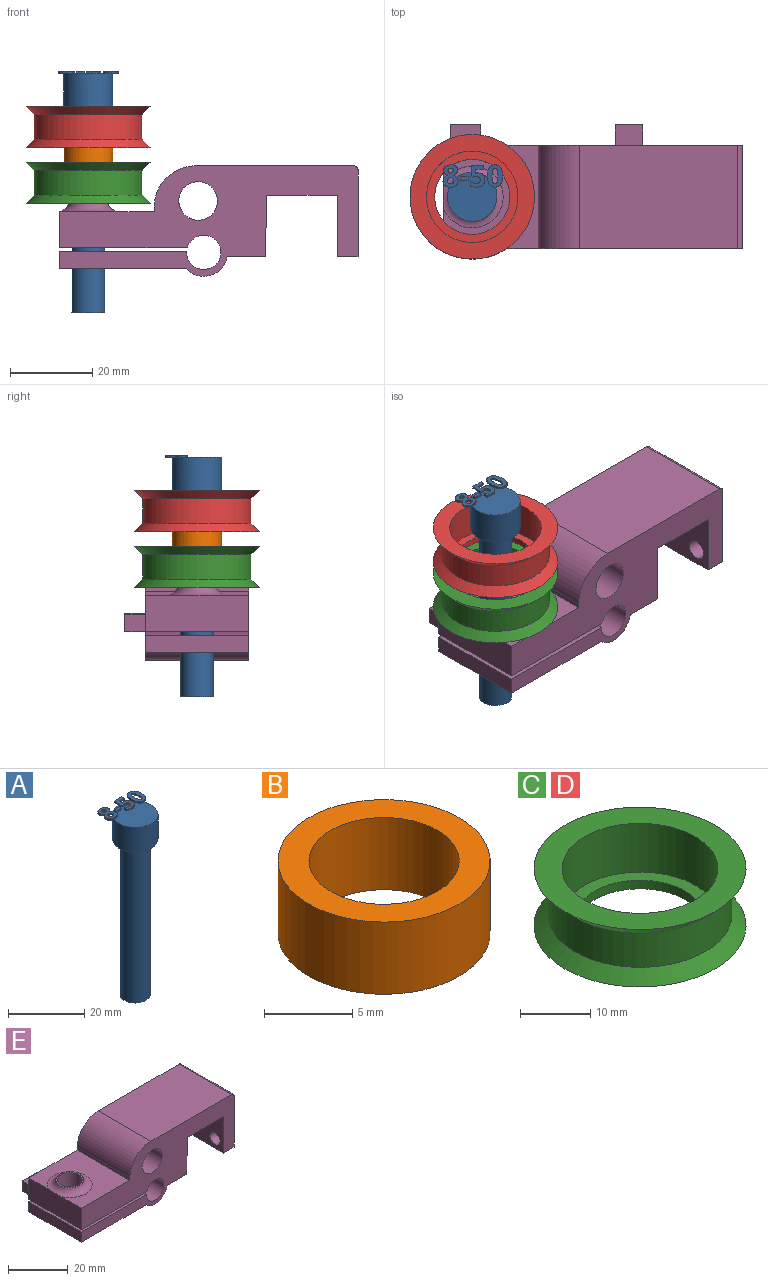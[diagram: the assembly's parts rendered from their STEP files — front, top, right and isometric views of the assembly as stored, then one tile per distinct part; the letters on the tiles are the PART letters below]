
ASSEMBLY  parts=5 mates=4
PART A: 86 faces, bbox 14.5x13.7x58.5 mm
  f0: plane 12x12mm, normal (0,0,1), area 99.4mm2, adj f5,f22,f23,f24,f25,f26,f40,f41
  f1: plane 1x0.26mm, normal (0,0,1), area 0.1mm2, adj f5,f46,f47,f48,f49
  f2: plane 0.85x0.68mm, normal (0,0,1), area 0.2mm2, adj f5,f29,f30,f31
  f3: cylinder r=4mm len=50mm, axis (0,0,-1), area 1256.6mm2, adj f4,f6
  f4: plane 8x8mm, normal (0,0,-1), area 50.3mm2, adj f3
  f5: cylinder r=6mm len=12mm, axis (0,0,-1), area 301.6mm2, adj f0,f1,f2,f6,f39,f45,f67,f85
  f6: plane 12x12mm, normal (0,0,-1), area 62.8mm2, adj f3,f5
  f7: extruded ~0.5x0.46mm, area 0.2mm2, adj f8,f37,f38,f39
  f8: extruded ~0.5x0.46mm, area 0.2mm2, adj f7,f9,f38,f39
  f9: extruded ~0.5x0.39mm, area 0.2mm2, adj f8,f10,f38,f39
  f10: extruded ~0.5x0.4mm, area 0.2mm2, adj f9,f11,f38,f39
  f11: extruded ~0.5x0.49mm, area 0.3mm2, adj f10,f12,f38,f39
  f12: extruded ~0.5x0.5mm, area 0.3mm2, adj f11,f13,f38,f39
  f13: extruded ~0.5x0.39mm, area 0.2mm2, adj f12,f37,f38,f39
  f14: extruded ~1.22x0.5mm, area 0.6mm2, adj f15,f35,f38,f39
  f15: extruded ~1.22x0.5mm, area 0.6mm2, adj f14,f16,f38,f39
  f16: extruded ~0.91x0.5mm, area 0.5mm2, adj f15,f17,f38,f39
  f17: extruded ~0.71x0.5mm, area 0.4mm2, adj f16,f18,f38,f39
  f18: extruded ~0.65x0.61mm, area 0.4mm2, adj f17,f19,f38,f39
  f19: extruded ~0.77x0.62mm, area 0.5mm2, adj f18,f20,f38,f39
  f20: extruded ~0.8x0.5mm, area 0.4mm2, adj f19,f21,f38,f39
  f21: extruded ~1.04x0.5mm, area 0.6mm2, adj f20,f22,f38,f39
  f22: extruded ~1.36x0.5mm, area 0.7mm2, adj f0,f21,f23,f38,f39
  f23: extruded ~1.33x0.5mm, area 0.7mm2, adj f0,f22,f24,f38
  f24: extruded ~1.04x0.51mm, area 0.6mm2, adj f0,f23,f25,f38
  f25: extruded ~0.75x0.5mm, area 0.4mm2, adj f0,f24,f26,f38
  f26: extruded ~0.85x0.66mm, area 0.5mm2, adj f0,f25,f27,f38,f39
  f27: extruded ~0.72x0.56mm, area 0.5mm2, adj f26,f28,f38,f39
  f28: extruded ~0.72x0.5mm, area 0.4mm2, adj f27,f35,f38,f39
  f29: extruded ~0.5x0.45mm, area 0.3mm2, adj f2,f30,f36,f38,f39
  f30: extruded ~0.5x0.47mm, area 0.3mm2, adj f2,f29,f31,f38
  f31: extruded ~0.62x0.5mm, area 0.3mm2, adj f2,f30,f32,f38,f39
  f32: extruded ~0.59x0.5mm, area 0.3mm2, adj f31,f33,f38,f39
  f33: extruded ~0.5x0.48mm, area 0.3mm2, adj f32,f34,f38,f39
  f34: extruded ~0.89x0.77mm, area 0.6mm2, adj f33,f36,f38,f39
  f35: extruded ~0.93x0.5mm, area 0.5mm2, adj f14,f28,f38,f39
  f36: extruded ~0.66x0.5mm, area 0.4mm2, adj f29,f34,f38,f39
  f37: extruded ~0.5x0.39mm, area 0.2mm2, adj f7,f13,f38,f39
  f38: plane 5.4x3.69mm, normal (0,0,1), area 12.7mm2, adj f7,f8,f9,f10,f11,f12,f13,f14
  f39: plane 5.4x3.53mm, normal (0,0,-1), area 10.2mm2, adj f5,f7,f8,f9,f10,f11,f12,f13
  f40: plane 0.9x0.5mm, normal (-1,0,0), area 0.4mm2, adj f0,f41,f43,f44
  f41: plane 1.93x0.5mm, normal (0,-1,0), area 1mm2, adj f0,f40,f42,f44
  f42: plane 0.9x0.5mm, normal (1,0,0), area 0.4mm2, adj f0,f41,f43,f44
  f43: plane 1.93x0.5mm, normal (0,1,0), area 1mm2, adj f0,f40,f42,f44
  f44: plane 1.93x0.9mm, normal (0,0,1), area 1.7mm2, adj f40,f41,f42,f43
  f45: plane 0.76x0.31mm, normal (0,0,-1), area 0mm2, adj f5,f46
  f46: extruded ~1.21x0.5mm, area 0.7mm2, adj f0,f1,f45,f47,f65,f66
  f47: extruded ~0.54x0.5mm, area 0.3mm2, adj f1,f46,f48,f66
  f48: plane 0.5x0.13mm, normal (-0.2,0.98,0), area 0.1mm2, adj f1,f47,f49,f66
  f49: plane 1.03x0.5mm, normal (1,-0.09,0), area 0.5mm2, adj f1,f48,f50,f66,f67
  f50: plane 1.88x0.5mm, normal (0,-1,0), area 0.9mm2, adj f49,f51,f66,f67
  f51: plane 0.94x0.5mm, normal (1,0,0), area 0.5mm2, adj f50,f52,f66,f67
  f52: plane 2.85x0.5mm, normal (0,1,0), area 1.4mm2, adj f51,f53,f66,f67
  f53: plane 2.68x0.5mm, normal (-1,0.07,0), area 1.3mm2, adj f0,f52,f54,f66,f67
  f54: plane 0.5x0.44mm, normal (-0.47,-0.88,0), area 0.3mm2, adj f0,f53,f55,f66
  f55: extruded ~0.5x0.37mm, area 0.2mm2, adj f0,f54,f56,f66
  f56: extruded ~0.5x0.42mm, area 0.2mm2, adj f0,f55,f57,f66
  f57: extruded ~1.05x0.8mm, area 0.8mm2, adj f0,f56,f58,f66
  f58: extruded ~1.02x0.83mm, area 0.8mm2, adj f0,f57,f59,f66
  f59: extruded ~0.72x0.5mm, area 0.4mm2, adj f0,f58,f60,f66
  f60: extruded ~0.66x0.5mm, area 0.4mm2, adj f0,f59,f61,f66
  f61: plane 0.96x0.5mm, normal (-1,0,0), area 0.5mm2, adj f0,f60,f62,f66
  f62: extruded ~1.42x0.5mm, area 0.7mm2, adj f0,f61,f63,f66
  f63: extruded ~1.55x0.5mm, area 0.8mm2, adj f0,f62,f64,f66
  f64: extruded ~1.36x0.54mm, area 0.8mm2, adj f0,f63,f65,f66
  f65: extruded ~1.17x0.5mm, area 0.6mm2, adj f0,f46,f64,f66
  f66: plane 5.33x3.51mm, normal (0,0,1), area 10.9mm2, adj f46,f47,f48,f49,f50,f51,f52,f53
  f67: plane 2.97x1.71mm, normal (0,0,-1), area 3.5mm2, adj f5,f49,f50,f51,f52,f53
  f68: extruded ~1.39x0.5mm, area 0.7mm2, adj f69,f83,f84,f85
  f69: extruded ~1.39x0.5mm, area 0.7mm2, adj f68,f70,f84,f85
  f70: extruded ~0.56x0.5mm, area 0.4mm2, adj f69,f71,f84,f85
  f71: extruded ~0.56x0.5mm, area 0.4mm2, adj f70,f72,f84,f85
  f72: extruded ~1.39x0.5mm, area 0.7mm2, adj f71,f73,f84,f85
  f73: extruded ~1.38x0.5mm, area 0.7mm2, adj f72,f74,f84,f85
  f74: extruded ~0.56x0.5mm, area 0.4mm2, adj f73,f83,f84,f85
  f75: extruded ~2.04x0.5mm, area 1.1mm2, adj f76,f82,f84,f85
  f76: extruded ~2.02x0.5mm, area 1.1mm2, adj f75,f77,f84,f85
  f77: extruded ~1.38x0.69mm, area 0.8mm2, adj f76,f78,f84,f85
  f78: extruded ~1.38x0.66mm, area 0.8mm2, adj f77,f79,f84,f85
  f79: extruded ~2.05x0.5mm, area 1.1mm2, adj f78,f80,f84,f85
  f80: extruded ~2.02x0.5mm, area 1mm2, adj f0,f79,f81,f84,f85
  f81: extruded ~1.37x0.68mm, area 0.8mm2, adj f0,f80,f82,f84
  f82: extruded ~1.39x0.66mm, area 0.8mm2, adj f0,f75,f81,f84,f85
  f83: extruded ~0.56x0.5mm, area 0.4mm2, adj f68,f74,f84,f85
  f84: plane 5.41x3.68mm, normal (0,0,1), area 12.1mm2, adj f68,f69,f70,f71,f72,f73,f74,f75
  f85: plane 5.41x3.68mm, normal (0,0,-1), area 10.3mm2, adj f5,f68,f69,f70,f71,f72,f73,f74
PART B: 4 faces, bbox 12x12x5 mm
  f0: cylinder r=4.25mm len=8.5mm, axis (0,0,-1), area 133.5mm2, adj f2,f3
  f1: cylinder r=6mm len=12mm, axis (0,0,-1), area 188.5mm2, adj f2,f3
  f2: plane 12x12mm, normal (0,0,1), area 56.4mm2, adj f0,f1
  f3: plane 12x12mm, normal (0,0,-1), area 56.4mm2, adj f0,f1
PART C: 8 faces, bbox 30.2x30.2x10 mm
  f0: plane 30.2x30.2mm, normal (0,0,1), area 329.2mm2, adj f1,f7
  f1: cylinder r=11.1mm len=22.2mm, axis (0,0,-1), area 592.8mm2, adj f0,f2
  f2: plane 22.2x22.2mm, normal (0,0,1), area 126.9mm2, adj f1,f3
  f3: cylinder r=9.1mm len=18.2mm, axis (0,0,-1), area 85.8mm2, adj f2,f4
  f4: plane 30.2x30.2mm, normal (0,0,-1), area 456.2mm2, adj f3,f5
  f5: cone r=13.1mm half-angle=45deg, axis (0,0,-1), area 250.6mm2, adj f4,f6
  f6: cylinder r=13.1mm len=26.2mm, axis (0,0,-1), area 493.9mm2, adj f5,f7
  f7: cone r=15.1mm half-angle=45deg, axis (0,0,1), area 250.6mm2, adj f0,f6
PART D: same geometry as C
PART E: 36 faces, bbox 75.9x30x26.8 mm
  f0: plane 25x4.13mm, normal (-1,0,0), area 103.3mm2, adj f3,f13,f14,f18
  f1: cylinder r=4.17mm len=8.35mm, axis (0,0,1), area 108.4mm2, adj f3,f18
  f2: plane 25x9.29mm, normal (0,0,-1), area 232.2mm2, adj f12,f13,f14,f16
  f3: plane 30.81x25mm, normal (0,0,-1), area 715.5mm2, adj f0,f1,f13,f14,f16
  f4: plane 25x8.81mm, normal (-1,0,0), area 219.3mm2, adj f5,f13,f14,f19,f23
  f5: plane 25x23mm, normal (0,0,1), area 400mm2, adj f4,f6,f13,f14,f23
  f6: plane 25x1.1mm, normal (-1,0,0), area 27.5mm2, adj f5,f13,f14,f24
  f7: plane 38.42x25mm, normal (0,0,1), area 960.6mm2, adj f13,f14,f24,f26
  f8: plane 25x21.09mm, normal (1,0,0), area 493.5mm2, adj f9,f13,f14,f21,f22,f26
  f9: plane 25x5mm, normal (0,0,-1), area 125mm2, adj f8,f10,f13,f14
  f10: plane 25x15mm, normal (-1,0,0), area 341.3mm2, adj f9,f11,f13,f14,f21,f22
  f11: plane 25x17.2mm, normal (0,0,-1), area 430mm2, adj f10,f12,f13,f14
  f12: plane 25x14.91mm, normal (1,0,-0.01), area 372.8mm2, adj f2,f11,f13,f14
  f13: plane 72.42x26.8mm, normal (0,-1,0), area 1035.8mm2, adj f0,f2,f3,f4,f5,f6,f7,f8
  f14: plane 72.42x26.8mm, normal (0,1,0), area 975.8mm2, adj f0,f2,f3,f4,f5,f6,f7,f8
  f15: cylinder r=4.17mm len=10.77mm, axis (0,0,1), area 282.4mm2, adj f19,f20
  f16: cylinder r=5.8mm len=25mm, axis (0,-1,0), area 320.1mm2, adj f2,f3,f13,f14
  f17: cylinder r=4.15mm len=25mm, axis (0,-1,0), area 626.5mm2, adj f13,f14,f18,f19
  f18: plane 30.86x25mm, normal (0,0,1), area 716.8mm2, adj f0,f1,f13,f14,f17
  f19: plane 31.02x30mm, normal (0,0,-1), area 757.2mm2, adj f4,f13,f14,f15,f17,f28,f29,f30
  f20: plane 9.35x9.35mm, normal (0,0,1), area 13.9mm2, adj f15,f23
  f21: cylinder r=2.43mm len=5mm, axis (1,0,0), area 76.2mm2, adj f8,f10
  f22: cylinder r=2.2mm len=5mm, axis (1,0,0), area 69.1mm2, adj f8,f10
  f23: torus R=7.5mm, axis (0,0,-1), area 134.6mm2, adj f4,f5,f20
  f24: cylinder r=10mm len=25mm, axis (0,-1,0), area 392.7mm2, adj f6,f7,f13,f14
  f25: cylinder r=4.68mm len=25mm, axis (0,-1,0), area 735.2mm2, adj f13,f14
  f26: cylinder r=1mm len=25mm, axis (0,-1,0), area 39.3mm2, adj f7,f8,f13,f14
  f27: plane 7.3x5mm, normal (0,0,1), area 36.5mm2, adj f14,f28,f29,f30
  f28: plane 5x4.12mm, normal (-1,0,0), area 20.6mm2, adj f14,f19,f27,f30
  f29: plane 5x4.12mm, normal (1,0,0), area 20.6mm2, adj f14,f19,f27,f30
  f30: plane 7.3x4.12mm, normal (0,1,0), area 30.1mm2, adj f19,f27,f28,f29
  f31: plane 6.63x5mm, normal (0,0,1), area 33.2mm2, adj f14,f32,f34,f35
  f32: plane 5x4.5mm, normal (-1,0,0), area 22.5mm2, adj f14,f31,f33,f35
  f33: plane 6.63x5mm, normal (0,0,-1), area 33.2mm2, adj f14,f32,f34,f35
  f34: plane 5x4.5mm, normal (1,0,0), area 22.5mm2, adj f14,f31,f33,f35
  f35: plane 6.63x4.5mm, normal (0,1,0), area 29.9mm2, adj f31,f32,f33,f34
PLACE A t=(-103.78,-12.5,-13.6)mm
PLACE B rot(axis=(1,0,0),180deg) t=(-103.78,-12.5,26.4)mm
PLACE C t=(-103.78,-12.5,18.1)mm
PLACE D t=(-103.78,-12.5,31.6)mm
PLACE E at identity
MATE fastened A.f3 <-> D.f1  axis (0,0,-1) through (-103.78,-12.5,36.4)mm
MATE fastened B.f0 <-> C.f1  axis (0,0,1) through (-103.78,-12.5,21.4)mm
MATE fastened C.f1 <-> E.f1  axis (0,0,-1) through (-103.78,-12.5,12.9)mm
MATE fastened D.f1 <-> B.f0  axis (0,0,-1) through (-103.78,-12.5,26.4)mm
